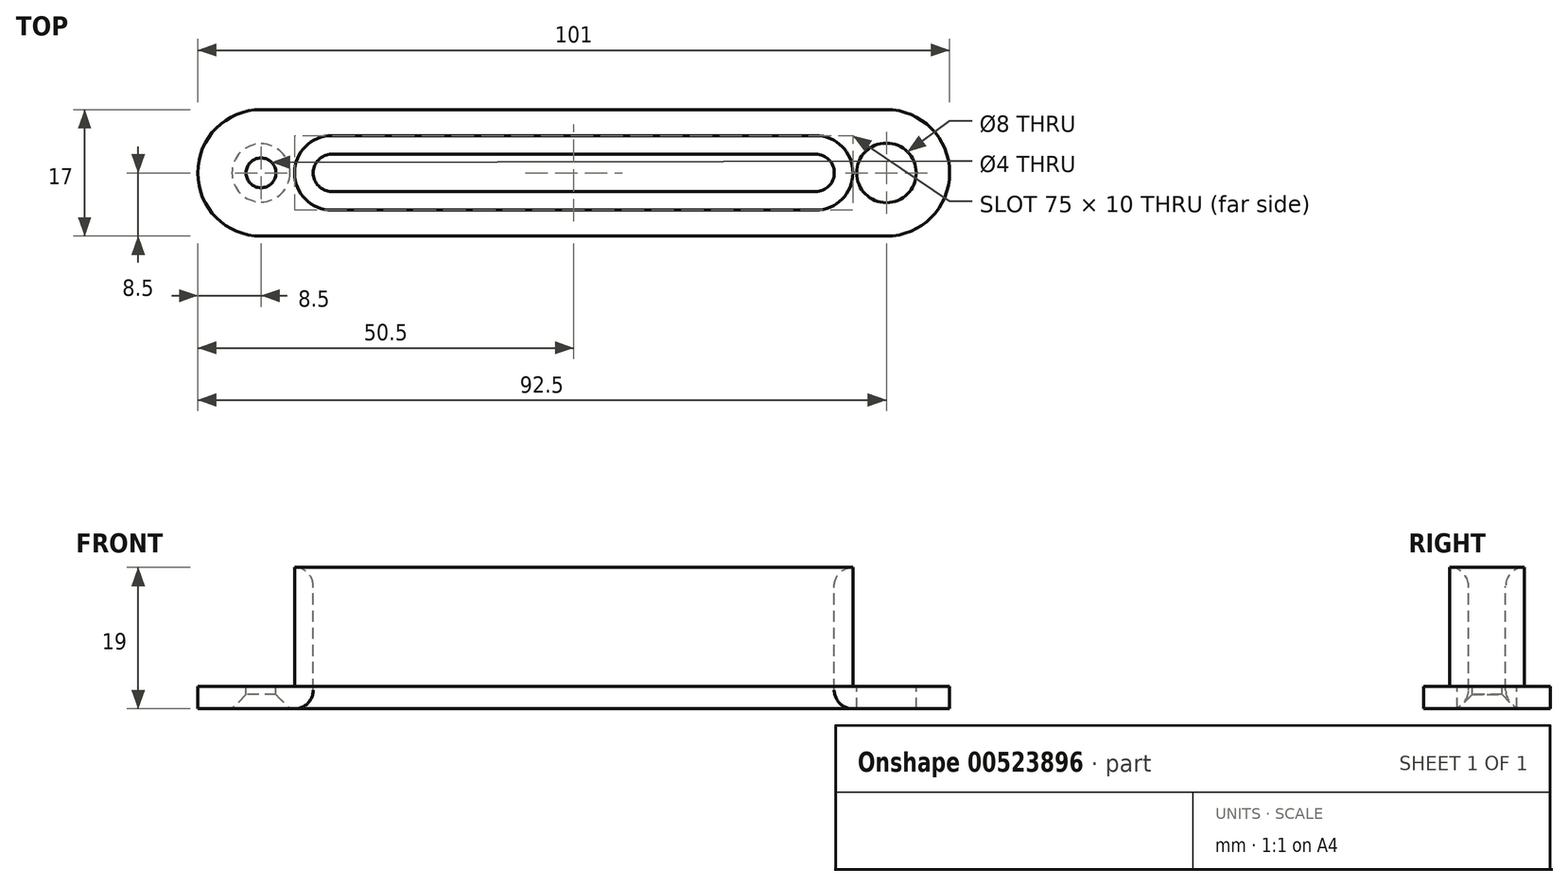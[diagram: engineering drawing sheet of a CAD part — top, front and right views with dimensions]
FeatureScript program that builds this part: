
annotation { "Feature Type Name" : "Feature", "Feature Type Description" : "" }
export const myFeature = defineFeature(function(context is Context, id is Id, definition is map)
    precondition{}
    {
        {
            var Q0;
            Q0=qCreatedBy(makeId("Top.planeOp"),FACE);
            var sketch = newSketch(context, id + "F0", { "sketchPlane" : qUnion([Q0])});
            skLineSegment(sketch, "E0.bottom", {"start": v(32.5, -2.5) * mm, "end": v(-32.5, -2.5) * mm});
            skLineSegment(sketch, "E0.top", {"start": v(32.5, 2.5) * mm, "end": v(-32.5, 2.5) * mm});
            skLineSegment(sketch, "E0.left", {"start": v(35, 0) * mm, "end": v(35, 0) * mm});
            skLineSegment(sketch, "E0.right", {"start": v(-35, 0) * mm, "end": v(-35, 0) * mm});
            skPoint(sketch, "E0.middle", {"position": v(0, 0) * mm});
            skLineSegment(sketch, "E1.0", {"start": v(-37.5, 0) * mm, "end": v(-37.5, 0) * mm});
            skLineSegment(sketch, "E1.1", {"start": v(32.5, -5) * mm, "end": v(-32.5, -5) * mm});
            skLineSegment(sketch, "E1.2", {"start": v(37.5, 0) * mm, "end": v(37.5, 0) * mm});
            skLineSegment(sketch, "E1.3", {"start": v(32.5, 5) * mm, "end": v(-32.5, 5) * mm});
            skLineSegment(sketch, "E2.0", {"start": v(42, 8.5) * mm, "end": v(-42, 8.5) * mm});
            skLineSegment(sketch, "E2.2", {"start": v(42, -8.5) * mm, "end": v(-42, -8.5) * mm});
            skLineSegment(sketch, "E3", {"start": v(0, 22.01) * mm, "end": v(0, -18.83) * mm, "construction": true});
            skPoint(sketch, "E3.startSnap0", {"position": v(0, 8.5) * mm});
            skArc(sketch, "E4", {"start": v(-42, 8.5) * mm, "mid": v(-50.5, 0) * mm, "end": v(-42, -8.5) * mm});
            skCircle(sketch, "E5", {"center": v(-42, 0) * mm, "radius": 2 * mm});
            skCircle(sketch, "E6", {"center": v(-42, 0) * mm, "radius": 4 * mm});
            skCircle(sketch, "E7.MirrorC", {"center": v(42, 0) * mm, "radius": 4 * mm});
            skCircle(sketch, "E8.MirrorC", {"center": v(42, 0) * mm, "radius": 2 * mm});
            skArc(sketch, "E9.MirrorCS", {"start": v(42, 8.5) * mm, "mid": v(50.5, 0) * mm, "end": v(42, -8.5) * mm});
            skPoint(sketch, "E10.visualSharp", {"position": v(-35, 2.5) * mm});
            skArc(sketch, "E10.filletArc", {"start": v(-32.5, 2.5) * mm, "mid": v(-34.27, 1.77) * mm, "end": v(-35, 0) * mm});
            skPoint(sketch, "E11.visualSharp", {"position": v(-35, -2.5) * mm});
            skArc(sketch, "E11.filletArc", {"start": v(-35, 0) * mm, "mid": v(-34.27, -1.77) * mm, "end": v(-32.5, -2.5) * mm});
            skPoint(sketch, "E12.visualSharp", {"position": v(35, 2.5) * mm});
            skArc(sketch, "E12.filletArc", {"start": v(35, 0) * mm, "mid": v(34.27, 1.77) * mm, "end": v(32.5, 2.5) * mm});
            skPoint(sketch, "E13.visualSharp", {"position": v(35, -2.5) * mm});
            skArc(sketch, "E13.filletArc", {"start": v(32.5, -2.5) * mm, "mid": v(34.27, -1.77) * mm, "end": v(35, 0) * mm});
            skPoint(sketch, "E14.visualSharp", {"position": v(37.5, -5) * mm});
            skArc(sketch, "E14.filletArc", {"start": v(32.5, -5) * mm, "mid": v(36.04, -3.54) * mm, "end": v(37.5, 0) * mm});
            skPoint(sketch, "E15.visualSharp", {"position": v(37.5, 5) * mm});
            skArc(sketch, "E15.filletArc", {"start": v(37.5, 0) * mm, "mid": v(36.04, 3.54) * mm, "end": v(32.5, 5) * mm});
            skPoint(sketch, "E16.visualSharp", {"position": v(-37.5, 5) * mm});
            skArc(sketch, "E16.filletArc", {"start": v(-32.5, 5) * mm, "mid": v(-36.04, 3.54) * mm, "end": v(-37.5, 0) * mm});
            skPoint(sketch, "E17.visualSharp", {"position": v(-37.5, -5) * mm});
            skArc(sketch, "E17.filletArc", {"start": v(-37.5, 0) * mm, "mid": v(-36.04, -3.54) * mm, "end": v(-32.5, -5) * mm});
            skSolve(sketch);
        }
        {
            var Q0;
            Q0=makeQuery(id+"F0.imprint","IMPRINT",FACE,{"disambiguationData":[TD([[makeQuery(id+"F0.imprint","IMPRINT",EDGE,{"derivedFrom":sQuery(id+"F0.wireOp",EDGE,"E0.bottom")}),-1.0]])]});
            var Q1;
            Q1=makeQuery(id+"F0.imprint","IMPRINT",FACE,{"disambiguationData":[TD([[makeQuery(id+"F0.imprint","IMPRINT",EDGE,{"derivedFrom":sQuery(id+"F0.wireOp",EDGE,"E1.1")}),1.0]])]});
            var Q2;
            Q2=makeQuery(id+"F0.imprint","IMPRINT",FACE,{"disambiguationData":[TD([[makeQuery(id+"F0.imprint","IMPRINT",EDGE,{"derivedFrom":sQuery(id+"F0.wireOp",EDGE,"E7.MirrorC")}),-1.0]])]});
            var Q3;
            Q3=makeQuery(id+"F0.imprint","IMPRINT",FACE,{"disambiguationData":[TD([[makeQuery(id+"F0.imprint","IMPRINT",EDGE,{"derivedFrom":sQuery(id+"F0.wireOp",EDGE,"E5")}),-1.0]])]});
            var Q4;
            Q4=makeQuery(id+"F0.imprint","IMPRINT",FACE,{"disambiguationData":[TD([[makeQuery(id+"F0.imprint","IMPRINT",EDGE,{"derivedFrom":sQuery(id+"F0.wireOp",EDGE,"E5")}),1.0]])]});
            var Q5;
            Q5=makeQuery(id+"F0.imprint","IMPRINT",FACE,{"disambiguationData":[TD([[makeQuery(id+"F0.imprint","IMPRINT",EDGE,{"derivedFrom":sQuery(id+"F0.wireOp",EDGE,"E8.MirrorC")}),-1.0]])]});
            var Q6;
            Q6=makeQuery(id+"F0.imprint","IMPRINT",FACE,{"disambiguationData":[TD([[makeQuery(id+"F0.imprint","IMPRINT",EDGE,{"derivedFrom":sQuery(id+"F0.wireOp",EDGE,"E0.bottom")}),1.0]])]});
            extrude(context, id + "F1", {"entities" : qUnion([Q0, Q1, Q2, Q3, Q4, Q5, Q6]), "depth" : 2 * mm});
        }
        {
            var Q0;
            Q0=makeQuery(id+"F0.imprint","IMPRINT",FACE,{"disambiguationData":[TD([[makeQuery(id+"F0.imprint","IMPRINT",EDGE,{"derivedFrom":sQuery(id+"F0.wireOp",EDGE,"E1.1")}),1.0]])]});
            var Q1;
            Q1=makeQuery(id+"F0.imprint","IMPRINT",FACE,{"disambiguationData":[TD([[makeQuery(id+"F0.imprint","IMPRINT",EDGE,{"derivedFrom":sQuery(id+"F0.wireOp",EDGE,"E0.bottom")}),1.0]])]});
            var Q2;
            Q2=makeQuery(id+"F0.imprint","IMPRINT",FACE,{"disambiguationData":[TD([[makeQuery(id+"F0.imprint","IMPRINT",EDGE,{"derivedFrom":sQuery(id+"F0.wireOp",EDGE,"E5")}),-1.0]])]});
            var Q3;
            Q3=makeQuery(id+"F0.imprint","IMPRINT",FACE,{"disambiguationData":[TD([[makeQuery(id+"F0.imprint","IMPRINT",EDGE,{"derivedFrom":sQuery(id+"F0.wireOp",EDGE,"E7.MirrorC")}),-1.0]])]});
            extrude(context, id + "F2", {"entities" : qUnion([Q0, Q1, Q2, Q3]), "operationType" : NewBodyOperationType.ADD, "oppositeDirection" : true, "depth" : 1 * mm});
        }
        {
            var Q0;
            Q0=makeQuery(id+"F0.imprint","IMPRINT",FACE,{"disambiguationData":[TD([[makeQuery(id+"F0.imprint","IMPRINT",EDGE,{"derivedFrom":sQuery(id+"F0.wireOp",EDGE,"E8.MirrorC")}),-1.0]])]});
            var Q1;
            Q1=makeQuery(id+"F0.imprint","IMPRINT",FACE,{"disambiguationData":[TD([[makeQuery(id+"F0.imprint","IMPRINT",EDGE,{"derivedFrom":sQuery(id+"F0.wireOp",EDGE,"E5")}),1.0]])]});
            extrude(context, id + "F3", {"entities" : qUnion([Q0, Q1]), "operationType" : NewBodyOperationType.REMOVE, "endBound" : BoundingType.THROUGH_ALL, "depth" : 25 * mm});
        }
        {
            var Q0;
            Q0=makeQuery(id+"F0.imprint","IMPRINT",FACE,{"disambiguationData":[TD([[makeQuery(id+"F0.imprint","IMPRINT",EDGE,{"derivedFrom":sQuery(id+"F0.wireOp",EDGE,"E0.bottom")}),1.0]])]});
            extrude(context, id + "F4", {"entities" : qUnion([Q0]), "operationType" : NewBodyOperationType.ADD, "depth" : 18 * mm});
        }
        {
            var Q0;
            Q0=makeQuery(id+"F0.imprint","IMPRINT",FACE,{"disambiguationData":[TD([[makeQuery(id+"F0.imprint","IMPRINT",EDGE,{"derivedFrom":sQuery(id+"F0.wireOp",EDGE,"E0.bottom")}),-1.0]])]});
            extrude(context, id + "F5", {"entities" : qUnion([Q0]), "operationType" : NewBodyOperationType.REMOVE, "endBound" : BoundingType.THROUGH_ALL, "depth" : 25 * mm});
        }
        {
            var Q0;
            Q0=makeQuery(id+"F2.opExtrude","CAP_EDGE",EDGE,{"disambiguationData":[OSD([sQuery(id+"F0.wireOp",EDGE,"E0.top")])],"isStart":false});
            var Q1;
            Q1=makeQuery(id+"F4.opExtrude","CAP_EDGE",EDGE,{"disambiguationData":[OSD([sQuery(id+"F0.wireOp",EDGE,"E0.bottom")])],"isStart":false});
            fillet(context, id + "F6", {"entities" : qUnion([Q0, Q1]), "radius" : 2.5 * mm, "tangentPropagation" : true, "allowEdgeOverflow" : false});
        }
        {
            var Q0;
            Q0=makeQuery(id+"F2.opExtrude","CAP_EDGE",EDGE,{"disambiguationData":[OSD([sQuery(id+"F0.wireOp",EDGE,"E5")])],"isStart":false});
            var Q1;
            Q1=makeQuery(id+"F2.opExtrude","CAP_EDGE",EDGE,{"disambiguationData":[OSD([sQuery(id+"F0.wireOp",EDGE,"E8.MirrorC")])],"isStart":false});
            chamfer(context, id + "F7", {"entities" : qUnion([Q0, Q1]), "width" : 1.9 * mm, "tangentPropagation" : true});
        }
    });
